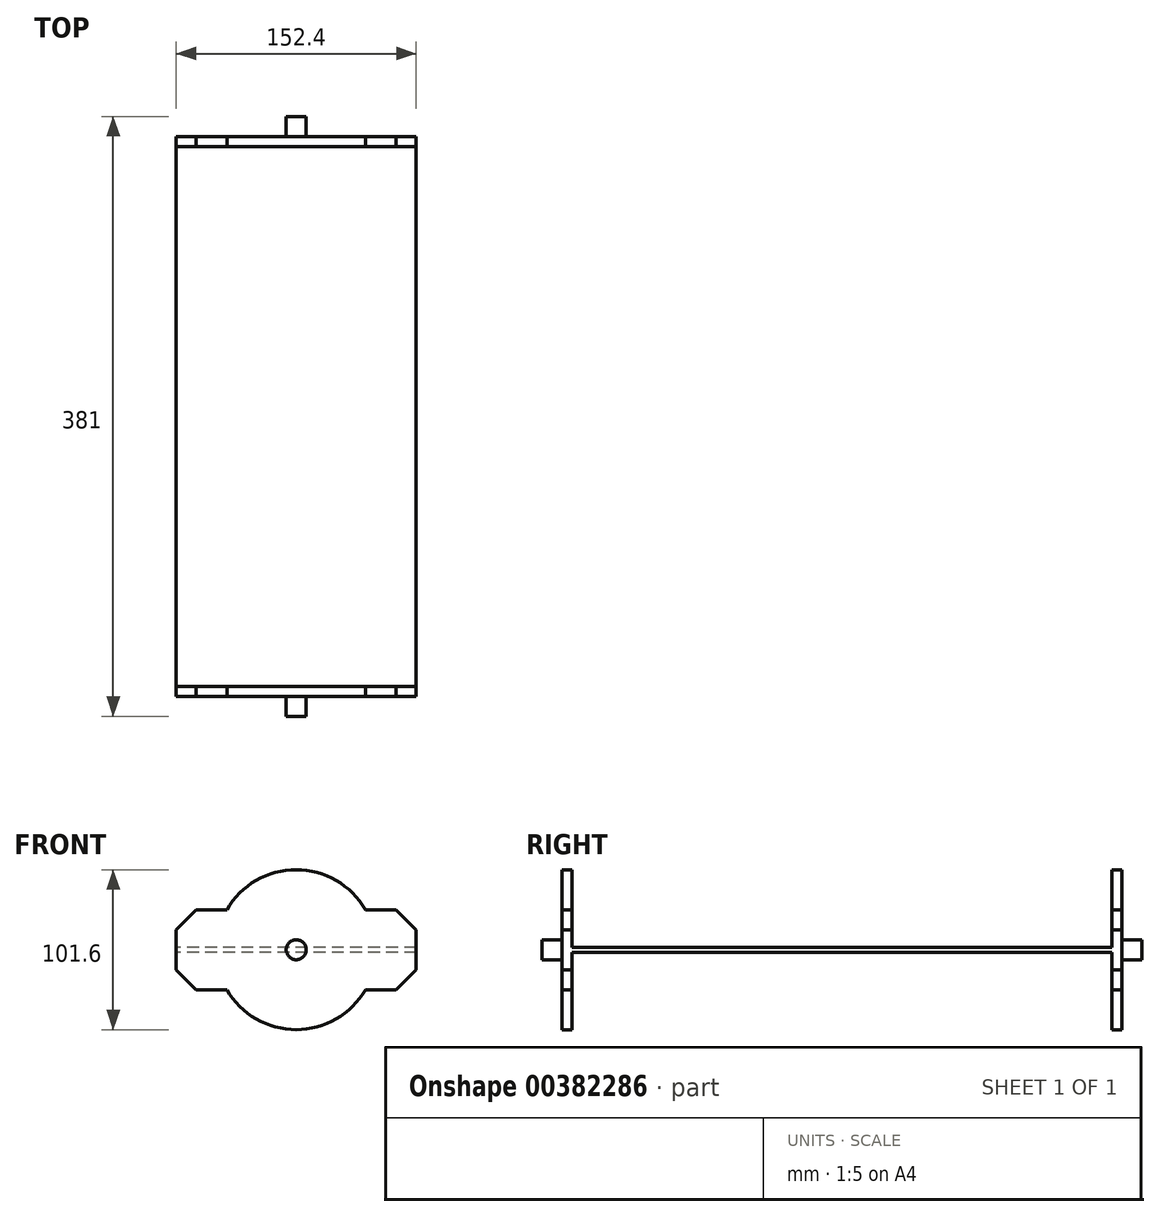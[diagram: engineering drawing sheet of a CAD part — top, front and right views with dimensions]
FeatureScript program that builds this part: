
annotation { "Feature Type Name" : "Feature", "Feature Type Description" : "" }
export const myFeature = defineFeature(function(context is Context, id is Id, definition is map)
    precondition{}
    {
        {
            var Q0;
            Q0=qCreatedBy(makeId("Front.planeOp"),FACE);
            var sketch = newSketch(context, id + "F0", { "sketchPlane" : qUnion([Q0])});
            skLineSegment(sketch, "E0.bottom", {"start": v(76.2, -38.1) * mm, "end": v(-76.2, -38.1) * mm});
            skLineSegment(sketch, "E0.top", {"start": v(76.2, 38.1) * mm, "end": v(-76.2, 38.1) * mm});
            skLineSegment(sketch, "E0.left", {"start": v(76.2, -38.1) * mm, "end": v(76.2, 38.1) * mm});
            skLineSegment(sketch, "E0.right", {"start": v(-76.2, -38.1) * mm, "end": v(-76.2, 38.1) * mm});
            skPoint(sketch, "E0.middle", {"position": v(0, 0) * mm});
            skLineSegment(sketch, "E1.bottom", {"start": v(76.2, -1.59) * mm, "end": v(-76.2, -1.59) * mm});
            skLineSegment(sketch, "E1.top", {"start": v(76.2, 1.59) * mm, "end": v(-76.2, 1.59) * mm});
            skLineSegment(sketch, "E1.left", {"start": v(76.2, -1.59) * mm, "end": v(76.2, 1.59) * mm});
            skLineSegment(sketch, "E1.right", {"start": v(-76.2, -1.59) * mm, "end": v(-76.2, 1.59) * mm});
            skSolve(sketch);
        }
        {
            var Q0;
            Q0=makeQuery(id+"F0.imprint","IMPRINT",FACE,{"disambiguationData":[TD([[makeQuery(id+"F0.imprint","IMPRINT",EDGE,{"derivedFrom":sQuery(id+"F0.wireOp",EDGE,"E1.bottom")}),-1.0]])]});
            extrude(context, id + "F1", {"entities" : qUnion([Q0]), "endBound" : BoundingType.SYMMETRIC, "depth" : 355.6 * mm});
        }
        {
            var Q0;
            Q0=qCreatedBy(makeId("Top.planeOp"),FACE);
            var sketch = newSketch(context, id + "F2", { "sketchPlane" : qUnion([Q0])});
            skLineSegment(sketch, "E2.bottom", {"start": v(76.2, 177.8) * mm, "end": v(-76.2, 177.8) * mm});
            skLineSegment(sketch, "E2.top", {"start": v(76.2, -177.8) * mm, "end": v(-76.2, -177.8) * mm});
            skLineSegment(sketch, "E2.left", {"start": v(76.2, 177.8) * mm, "end": v(76.2, -177.8) * mm});
            skLineSegment(sketch, "E2.right", {"start": v(-76.2, 177.8) * mm, "end": v(-76.2, -177.8) * mm});
            skPoint(sketch, "E2.middle", {"position": v(0, 0) * mm});
            skLineSegment(sketch, "E3.0", {"start": v(76.2, -171.45) * mm, "end": v(-76.2, -171.45) * mm});
            skLineSegment(sketch, "E4.0", {"start": v(76.2, 171.45) * mm, "end": v(-76.2, 171.45) * mm});
            skSolve(sketch);
        }
        {
            var Q0;
            {var subQ0=sQuery(id+"F2.wireOp",EDGE,"E2.top");Q0=makeQuery(id+"F2.imprint","IMPRINT",FACE,{"disambiguationData":[TD([[makeQuery(id+"F2.imprint","IMPRINT",EDGE,{"derivedFrom":subQ0}),-1.0]])]});}
            var Q1;
            {var subQ0=sQuery(id+"F2.wireOp",EDGE,"E2.bottom");Q1=makeQuery(id+"F2.imprint","IMPRINT",FACE,{"disambiguationData":[TD([[makeQuery(id+"F2.imprint","IMPRINT",EDGE,{"derivedFrom":subQ0}),1.0]])]});}
            extrude(context, id + "F3", {"entities" : qUnion([Q0, Q1]), "operationType" : NewBodyOperationType.ADD, "endBound" : BoundingType.SYMMETRIC, "depth" : 50.8 * mm});
        }
        {
            var Q0;
            {var subQ0=sQuery(id+"F2.wireOp",EDGE,"E2.left");Q0=makeQuery(id+"F3.opExtrude","CAP_EDGE",EDGE,{"disambiguationData":[OSD([subQ0]),TDD([makeQuery(id+"F2.imprint","IMPRINT",EDGE,{"disambiguationData":[TD([[makeQuery(id+"F2.imprint","INTERSECT",VERTEX,{"derivedFrom":[sQuery(id+"F2.wireOp",EDGE,"E2.top"),subQ0]}),1.0]])],"derivedFrom":subQ0})])],"isStart":false});}
            var Q1;
            {var subQ0=sQuery(id+"F2.wireOp",EDGE,"E2.right");Q1=makeQuery(id+"F3.opExtrude","CAP_EDGE",EDGE,{"disambiguationData":[OSD([subQ0]),TDD([makeQuery(id+"F2.imprint","IMPRINT",EDGE,{"disambiguationData":[TD([[makeQuery(id+"F2.imprint","INTERSECT",VERTEX,{"derivedFrom":[sQuery(id+"F2.wireOp",EDGE,"E2.top"),subQ0]}),1.0]])],"derivedFrom":subQ0})])],"isStart":false});}
            var Q2;
            {var subQ0=sQuery(id+"F2.wireOp",EDGE,"E2.right");Q2=makeQuery(id+"F3.opExtrude","CAP_EDGE",EDGE,{"disambiguationData":[OSD([subQ0]),TDD([makeQuery(id+"F2.imprint","IMPRINT",EDGE,{"disambiguationData":[TD([[makeQuery(id+"F2.imprint","INTERSECT",VERTEX,{"derivedFrom":[sQuery(id+"F2.wireOp",EDGE,"E2.top"),subQ0]}),1.0]])],"derivedFrom":subQ0})])],"isStart":true});}
            var Q3;
            {var subQ0=sQuery(id+"F2.wireOp",EDGE,"E2.left");Q3=makeQuery(id+"F3.opExtrude","CAP_EDGE",EDGE,{"disambiguationData":[OSD([subQ0]),TDD([makeQuery(id+"F2.imprint","IMPRINT",EDGE,{"disambiguationData":[TD([[makeQuery(id+"F2.imprint","INTERSECT",VERTEX,{"derivedFrom":[sQuery(id+"F2.wireOp",EDGE,"E2.top"),subQ0]}),1.0]])],"derivedFrom":subQ0})])],"isStart":true});}
            var Q4;
            {var subQ0=sQuery(id+"F2.wireOp",EDGE,"E2.left");Q4=makeQuery(id+"F3.opExtrude","CAP_EDGE",EDGE,{"disambiguationData":[OSD([subQ0]),TDD([makeQuery(id+"F2.imprint","IMPRINT",EDGE,{"disambiguationData":[TD([[makeQuery(id+"F2.imprint","INTERSECT",VERTEX,{"derivedFrom":[sQuery(id+"F2.wireOp",EDGE,"E2.bottom"),subQ0]}),-1.0]])],"derivedFrom":subQ0})])],"isStart":false});}
            var Q5;
            {var subQ0=sQuery(id+"F2.wireOp",EDGE,"E2.right");Q5=makeQuery(id+"F3.opExtrude","CAP_EDGE",EDGE,{"disambiguationData":[OSD([subQ0]),TDD([makeQuery(id+"F2.imprint","IMPRINT",EDGE,{"disambiguationData":[TD([[makeQuery(id+"F2.imprint","INTERSECT",VERTEX,{"derivedFrom":[sQuery(id+"F2.wireOp",EDGE,"E2.bottom"),subQ0]}),-1.0]])],"derivedFrom":subQ0})])],"isStart":false});}
            var Q6;
            {var subQ0=sQuery(id+"F2.wireOp",EDGE,"E2.left");Q6=makeQuery(id+"F3.opExtrude","CAP_EDGE",EDGE,{"disambiguationData":[OSD([subQ0]),TDD([makeQuery(id+"F2.imprint","IMPRINT",EDGE,{"disambiguationData":[TD([[makeQuery(id+"F2.imprint","INTERSECT",VERTEX,{"derivedFrom":[sQuery(id+"F2.wireOp",EDGE,"E2.bottom"),subQ0]}),-1.0]])],"derivedFrom":subQ0})])],"isStart":true});}
            var Q7;
            {var subQ0=sQuery(id+"F2.wireOp",EDGE,"E2.right");Q7=makeQuery(id+"F3.opExtrude","CAP_EDGE",EDGE,{"disambiguationData":[OSD([subQ0]),TDD([makeQuery(id+"F2.imprint","IMPRINT",EDGE,{"disambiguationData":[TD([[makeQuery(id+"F2.imprint","INTERSECT",VERTEX,{"derivedFrom":[sQuery(id+"F2.wireOp",EDGE,"E2.bottom"),subQ0]}),-1.0]])],"derivedFrom":subQ0})])],"isStart":true});}
            chamfer(context, id + "F4", {"entities" : qUnion([Q0, Q1, Q2, Q3, Q4, Q5, Q6, Q7]), "width" : 12.7 * mm, "tangentPropagation" : true});
        }
        {
            var Q0;
            Q0=makeQuery(id+"F3.boolean.opBoolean","MERGE",FACE,{"derivedFrom":[makeQuery(id+"F1.opExtrude","CAP_FACE",FACE,{"disambiguationData":[OSD([sQuery(id+"F0.wireOp",EDGE,"E1.bottom"),sQuery(id+"F0.wireOp",EDGE,"E1.top"),sQuery(id+"F0.wireOp",EDGE,"E1.left"),sQuery(id+"F0.wireOp",EDGE,"E1.right")])],"isStart":true}),makeQuery(id+"F3.opExtrude","SWEPT_FACE",FACE,{"disambiguationData":[OSD([sQuery(id+"F2.wireOp",EDGE,"E2.bottom")])]})]});
            var sketch = newSketch(context, id + "F5", { "sketchPlane" : qUnion([Q0])});
            skCircle(sketch, "E5", {"center": v(0, 0) * mm, "radius": 6.35 * mm});
            skSolve(sketch);
        }
        {
            var Q0;
            Q0 = qSketchRegion(id + "F5", true);
            extrude(context, id + "F6", {"entities" : qUnion([Q0]), "operationType" : NewBodyOperationType.ADD, "depth" : 12.7 * mm});
        }
        {
            var Q0;
            Q0=makeQuery(id+"F3.boolean.opBoolean","MERGE",FACE,{"derivedFrom":[makeQuery(id+"F1.opExtrude","CAP_FACE",FACE,{"disambiguationData":[OSD([sQuery(id+"F0.wireOp",EDGE,"E1.bottom"),sQuery(id+"F0.wireOp",EDGE,"E1.top"),sQuery(id+"F0.wireOp",EDGE,"E1.left"),sQuery(id+"F0.wireOp",EDGE,"E1.right")])],"isStart":false}),makeQuery(id+"F3.opExtrude","SWEPT_FACE",FACE,{"disambiguationData":[OSD([sQuery(id+"F2.wireOp",EDGE,"E2.top")])]})]});
            var sketch = newSketch(context, id + "F7", { "sketchPlane" : qUnion([Q0])});
            skCircle(sketch, "E6", {"center": v(0, 0) * mm, "radius": 6.35 * mm});
            skSolve(sketch);
        }
        {
            var Q0;
            Q0 = qSketchRegion(id + "F7", true);
            extrude(context, id + "F8", {"entities" : qUnion([Q0]), "operationType" : NewBodyOperationType.ADD, "depth" : 12.7 * mm});
        }
        {
            var Q0;
            Q0=makeQuery(id+"F3.boolean.opBoolean","MERGE",FACE,{"derivedFrom":[makeQuery(id+"F1.opExtrude","CAP_FACE",FACE,{"disambiguationData":[OSD([sQuery(id+"F0.wireOp",EDGE,"E1.bottom"),sQuery(id+"F0.wireOp",EDGE,"E1.top"),sQuery(id+"F0.wireOp",EDGE,"E1.left"),sQuery(id+"F0.wireOp",EDGE,"E1.right")])],"isStart":false}),makeQuery(id+"F3.opExtrude","SWEPT_FACE",FACE,{"disambiguationData":[OSD([sQuery(id+"F2.wireOp",EDGE,"E2.top")])]})]});
            var sketch = newSketch(context, id + "F9", { "sketchPlane" : qUnion([Q0])});
            skCircle(sketch, "E7", {"center": v(0, 0) * mm, "radius": 50.8 * mm});
            skSolve(sketch);
        }
        {
            var Q0;
            Q0 = qSketchRegion(id + "F9", true);
            extrude(context, id + "F10", {"entities" : qUnion([Q0]), "operationType" : NewBodyOperationType.ADD, "oppositeDirection" : true, "depth" : 6.35 * mm});
        }
        {
            var Q0;
            Q0=makeQuery(id+"F3.boolean.opBoolean","MERGE",FACE,{"derivedFrom":[makeQuery(id+"F1.opExtrude","CAP_FACE",FACE,{"disambiguationData":[OSD([sQuery(id+"F0.wireOp",EDGE,"E1.bottom"),sQuery(id+"F0.wireOp",EDGE,"E1.top"),sQuery(id+"F0.wireOp",EDGE,"E1.left"),sQuery(id+"F0.wireOp",EDGE,"E1.right")])],"isStart":true}),makeQuery(id+"F3.opExtrude","SWEPT_FACE",FACE,{"disambiguationData":[OSD([sQuery(id+"F2.wireOp",EDGE,"E2.bottom")])]})]});
            var sketch = newSketch(context, id + "F11", { "sketchPlane" : qUnion([Q0])});
            skCircle(sketch, "E8", {"center": v(0, 0) * mm, "radius": 50.8 * mm});
            skSolve(sketch);
        }
        {
            var Q0;
            Q0 = qSketchRegion(id + "F11", true);
            extrude(context, id + "F12", {"entities" : qUnion([Q0]), "operationType" : NewBodyOperationType.ADD, "oppositeDirection" : true, "depth" : 6.35 * mm});
        }
    });
